# Revit family: LQ6235551_Jabonera Ducha Liquid Mate Black
name_source: partatom
category: Furniture
units: mm (PartAtom-declared; Revit-internal decimal feet)

## family parameters
Always vertical = Yes
Cut with Voids When Loaded = No
Host = Wall
OmniClass Number = 23.31.25.29.11
OmniClass Title = Hand Soap Holders
Room Calculation Point = No
Shared = No

## types (1)
- Type 1
    Alto = 20 mm
    Altura = 900 mm  [stored 2.95276 ft]
    Ancho = 260 mm  [stored 0.853018 ft]
    Colección = Liquid
    Componentes = Percha - Toallero - Jabonera - Barra - Cepillera - Portarrollo
    Creado por = IDD
    Description = La jabonera ducha Liquid, galardonada con el premio de diseño internacional Red Dot Design Award, es la mejor forma de modernizar tu baño y darle un toque único, mientras te proporciona seguridad y funcionalidad con una resistencia de hasta 9 kilos de carga. ¡Adquiérela ahora!
    Fecha de creación = 9/10/2020
    Garantía = 30 años en estructura
    Garantía Acabados = 5 años en acabados
    Línea = Liquid
    Manufacturer = Corona
    Material = Corona_Mate_Black
    Número de piezas = 6
    Profundidad = 105 mm  [stored 0.344488 ft]
    Referencia = LQ6060001
    Resistencia = Resistente a la corrosión
pelado y decoloración por agua
Resistencia al peso general hasta 9 kg
Resistencia al peso del toallero barra hasta 23 kg
    Tecnologías = DuraCrome
    URL = https://corona.co
    Uso = Residencial

note: [stored X ft] marks values corroborated as IEEE doubles in the binary element streams (Revit-internal decimal feet)

## geometry (parser evidence)
native form markers: Sweep x7
no freeform markers — native parametric forms only
